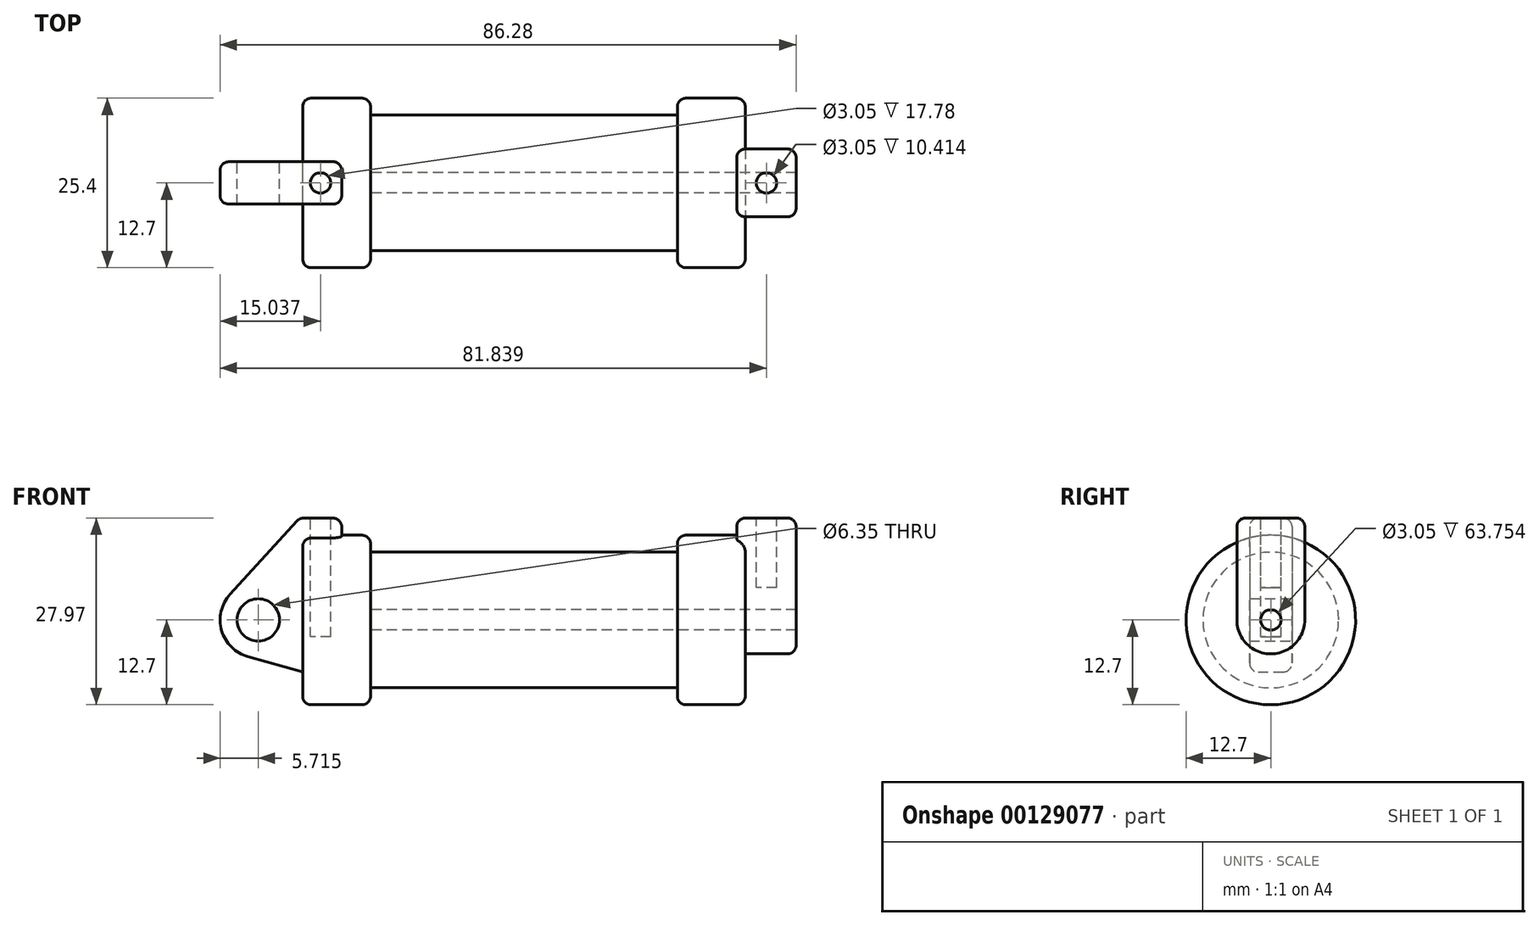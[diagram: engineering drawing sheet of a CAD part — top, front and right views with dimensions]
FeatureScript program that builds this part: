
annotation { "Feature Type Name" : "Feature", "Feature Type Description" : "" }
export const myFeature = defineFeature(function(context is Context, id is Id, definition is map)
    precondition{}
    {
        {
            var Q0;
            Q0=qCreatedBy(makeId("Front.planeOp"),FACE);
            var sketch = newSketch(context, id + "F0", { "sketchPlane" : qUnion([Q0])});
            skLineSegment(sketch, "E0", {"start": v(0, 0) * mm, "end": v(0, 12.7) * mm});
            skLineSegment(sketch, "E1", {"start": v(0, 12.7) * mm, "end": v(10.16, 12.7) * mm});
            skLineSegment(sketch, "E2", {"start": v(10.16, 12.7) * mm, "end": v(10.16, 10.16) * mm});
            skLineSegment(sketch, "E3", {"start": v(10.16, 10.16) * mm, "end": v(56.13, 10.16) * mm});
            skLineSegment(sketch, "E4", {"start": v(56.13, 10.16) * mm, "end": v(56.13, 12.7) * mm});
            skLineSegment(sketch, "E5", {"start": v(56.13, 12.7) * mm, "end": v(66.3, 12.7) * mm});
            skLineSegment(sketch, "E6", {"start": v(66.3, 12.7) * mm, "end": v(66.3, 0) * mm});
            skLineSegment(sketch, "E7", {"start": v(66.3, 0) * mm, "end": v(0, 0) * mm});
            skLineSegment(sketch, "E8", {"start": v(5.84, 15.24) * mm, "end": v(-0.5, 15.24) * mm});
            skLineSegment(sketch, "E9", {"start": v(-0.5, 15.24) * mm, "end": v(-10.88, 3.85) * mm});
            skLineSegment(sketch, "E10", {"start": v(0, 0) * mm, "end": v(-6.65, 0) * mm});
            skCircle(sketch, "E11", {"center": v(-6.65, 0) * mm, "radius": 5.72 * mm});
            skCircle(sketch, "E12", {"center": v(-6.65, 0) * mm, "radius": 3.18 * mm});
            skLineSegment(sketch, "E13", {"start": v(5.84, 15.24) * mm, "end": v(5.84, -9.4) * mm});
            skLineSegment(sketch, "E14", {"start": v(5.84, -9.4) * mm, "end": v(-8.18, -5.5) * mm});
            skSolve(sketch);
        }
        {
            var Q0;
            {var subQ0=sQuery(id+"F0.wireOp",EDGE,"E2");Q0=makeQuery(id+"F0.imprint","IMPRINT",FACE,{"disambiguationData":[TD([[makeQuery(id+"F0.imprint","IMPRINT",EDGE,{"derivedFrom":subQ0}),-1.0]])]});}
            var Q1;
            {var subQ0=sQuery(id+"F0.wireOp",EDGE,"E0");Q1=makeQuery(id+"F0.imprint","IMPRINT",FACE,{"disambiguationData":[TD([[makeQuery(id+"F0.imprint","IMPRINT",EDGE,{"derivedFrom":subQ0}),-1.0]])]});}
            var Q2;
            Q2=sQuery(id+"F0.wireOp",EDGE,"E7");
            revolve(context, id + "F1", {"entities" : qUnion([Q0, Q1]), "axis" : qUnion([Q2]), "revolveType" : RevolveType.FULL});
        }
        {
            var Q0;
            {var subQ4=sQuery(id+"F0.wireOp",EDGE,"E12");Q0=makeQuery(id+"F0.imprint","IMPRINT",FACE,{"disambiguationData":[TD([[makeQuery(id+"F0.imprint","IMPRINT",EDGE,{"derivedFrom":subQ4}),-1.0]])]});}
            var Q1;
            {var subQ0=sQuery(id+"F0.wireOp",EDGE,"E0");Q1=makeQuery(id+"F0.imprint","IMPRINT",FACE,{"disambiguationData":[TD([[makeQuery(id+"F0.imprint","IMPRINT",EDGE,{"derivedFrom":subQ0}),-1.0]])]});}
            var Q2;
            {var subQ3=sQuery(id+"F0.wireOp",EDGE,"E0");Q2=makeQuery(id+"F0.imprint","IMPRINT",FACE,{"disambiguationData":[TD([[makeQuery(id+"F0.imprint","IMPRINT",EDGE,{"derivedFrom":subQ3}),1.0]])]});}
            var Q3;
            {var subQ0=sQuery(id+"F0.wireOp",EDGE,"E14");Q3=makeQuery(id+"F0.imprint","IMPRINT",FACE,{"disambiguationData":[TD([[makeQuery(id+"F0.imprint","IMPRINT",EDGE,{"derivedFrom":subQ0}),-1.0]])]});}
            extrude(context, id + "F2", {"entities" : qUnion([Q0, Q1, Q2, Q3]), "operationType" : NewBodyOperationType.ADD, "endBound" : BoundingType.SYMMETRIC, "depth" : 6.35 * mm});
        }
        {
            var Q0;
            Q0=makeQuery(id+"F1.opRevolve","SWEPT_FACE",FACE,{"disambiguationData":[OSD([sQuery(id+"F0.wireOp",EDGE,"E6")])]});
            var sketch = newSketch(context, id + "F3", { "sketchPlane" : qUnion([Q0])});
            skCircle(sketch, "E15", {"center": v(0, 0) * mm, "radius": 1.52 * mm});
            skCircle(sketch, "E16", {"center": v(0, 0) * mm, "radius": 5.08 * mm});
            skLineSegment(sketch, "E17", {"start": v(-5.08, 0.03) * mm, "end": v(-5.08, 15.27) * mm});
            skLineSegment(sketch, "E18", {"start": v(-5.08, 15.27) * mm, "end": v(5.08, 15.27) * mm});
            skLineSegment(sketch, "E19", {"start": v(5.08, 15.27) * mm, "end": v(5.08, 0.03) * mm});
            skLineSegment(sketch, "E20", {"start": v(-1.52, -0.03) * mm, "end": v(1.52, -0.03) * mm});
            skSolve(sketch);
        }
        {
            var Q0;
            Q0 = qSketchRegion(id + "F3", true);
            extrude(context, id + "F4", {"entities" : qUnion([Q0]), "operationType" : NewBodyOperationType.ADD, "depth" : 7.62 * mm, "hasSecondDirection" : true, "secondDirectionOppositeDirection" : true, "secondDirectionDepth" : 1.27 * mm});
        }
        {
            var Q0;
            Q0=makeQuery(id+"F4.boolean.opBoolean","SPLIT",FACE,{"disambiguationData":[TD([makeQuery(id+"F4.opExtrude","SWEPT_FACE",FACE,{"disambiguationData":[OSD([sQuery(id+"F3.wireOp",EDGE,"E15")])]})])],"derivedFrom":makeQuery(id+"F1.opRevolve","SWEPT_FACE",FACE,{"disambiguationData":[OSD([sQuery(id+"F0.wireOp",EDGE,"E6")])]})});
            var Q1;
            Q1=makeQuery(id+"F1.opRevolve","SWEPT_FACE",FACE,{"disambiguationData":[OSD([sQuery(id+"F0.wireOp",EDGE,"E2")])]});
            extrude(context, id + "F5", {"entities" : qUnion([Q0]), "operationType" : NewBodyOperationType.REMOVE, "endBound" : BoundingType.UP_TO_SURFACE, "oppositeDirection" : true, "endBoundEntityFace" : qUnion([Q1]), "depth" : 25.4 * mm});
        }
        {
            var Q0;
            Q0=makeQuery(id+"F2.opExtrude","SWEPT_FACE",FACE,{"disambiguationData":[OSD([sQuery(id+"F0.wireOp",EDGE,"E8")])]});
            var sketch = newSketch(context, id + "F6", { "sketchPlane" : qUnion([Q0])});
            skCircle(sketch, "E21", {"center": v(2.67, 0) * mm, "radius": 1.52 * mm});
            skPoint(sketch, "E21.centerSnap0", {"position": v(2.67, 3.18) * mm});
            skSolve(sketch);
        }
        {
            var Q0;
            Q0=makeQuery(id+"F4.opExtrude","SWEPT_FACE",FACE,{"disambiguationData":[OSD([sQuery(id+"F3.wireOp",EDGE,"E18")])]});
            var sketch = newSketch(context, id + "F7", { "sketchPlane" : qUnion([Q0])});
            skCircle(sketch, "E22", {"center": v(69.47, 0) * mm, "radius": 1.52 * mm});
            skSolve(sketch);
        }
        {
            var Q0;
            Q0=makeQuery(id+"F6.imprint","IMPRINT",FACE,{"disambiguationData":[TD([[makeQuery(id+"F6.imprint","IMPRINT",EDGE,{"derivedFrom":sQuery(id+"F6.wireOp",EDGE,"E21")}),1.0]])]});
            extrude(context, id + "F8", {"entities" : qUnion([Q0]), "operationType" : NewBodyOperationType.REMOVE, "oppositeDirection" : true, "depth" : 17.78 * mm});
        }
        {
            var Q0;
            Q0=makeQuery(id+"F7.imprint","IMPRINT",FACE,{"disambiguationData":[TD([[makeQuery(id+"F7.imprint","IMPRINT",EDGE,{"derivedFrom":sQuery(id+"F7.wireOp",EDGE,"E22")}),1.0]])]});
            extrude(context, id + "F9", {"entities" : qUnion([Q0]), "operationType" : NewBodyOperationType.REMOVE, "oppositeDirection" : true, "depth" : 10.4 * mm});
        }
        {
            var Q0;
            Q0=makeQuery(id+"F2.opExtrude","CAP_EDGE",EDGE,{"disambiguationData":[OSD([sQuery(id+"F0.wireOp",EDGE,"E8")])],"isStart":false});
            var Q1;
            Q1=makeQuery(id+"F2.opExtrude","SWEPT_EDGE",EDGE,{"disambiguationData":[OSD([sQuery(id+"F0.wireOp",EDGE,"E8"),sQuery(id+"F0.wireOp",EDGE,"E9")])]});
            var Q2;
            Q2=makeQuery(id+"F2.opExtrude","CAP_EDGE",EDGE,{"disambiguationData":[OSD([sQuery(id+"F0.wireOp",EDGE,"E8")])],"isStart":true});
            var Q3;
            Q3=makeQuery(id+"F2.opExtrude","SWEPT_EDGE",EDGE,{"disambiguationData":[OSD([sQuery(id+"F0.wireOp",EDGE,"E8"),sQuery(id+"F0.wireOp",EDGE,"E13")])]});
            var Q4;
            Q4=makeQuery(id+"F2.opExtrude","CAP_EDGE",EDGE,{"disambiguationData":[OSD([sQuery(id+"F0.wireOp",EDGE,"E13")])],"isStart":true});
            var Q5;
            Q5=makeQuery(id+"F2.opExtrude","CAP_EDGE",EDGE,{"disambiguationData":[OSD([sQuery(id+"F0.wireOp",EDGE,"E13")])],"isStart":false});
            var Q6;
            Q6=makeQuery(id+"F2.opExtrude","CAP_EDGE",EDGE,{"disambiguationData":[OSD([sQuery(id+"F0.wireOp",EDGE,"E9")])],"isStart":true});
            var Q7;
            Q7=makeQuery(id+"F2.opExtrude","CAP_EDGE",EDGE,{"disambiguationData":[OSD([sQuery(id+"F0.wireOp",EDGE,"E9")])],"isStart":false});
            var Q8;
            Q8=makeQuery(id+"F1.opRevolve","SWEPT_EDGE",EDGE,{"disambiguationData":[OSD([sQuery(id+"F0.wireOp",EDGE,"E0"),sQuery(id+"F0.wireOp",EDGE,"E1")])]});
            var Q9;
            Q9=makeQuery(id+"F1.opRevolve","SWEPT_EDGE",EDGE,{"disambiguationData":[OSD([sQuery(id+"F0.wireOp",EDGE,"E1"),sQuery(id+"F0.wireOp",EDGE,"E2")])]});
            var Q10;
            Q10=makeQuery(id+"F1.opRevolve","SWEPT_EDGE",EDGE,{"disambiguationData":[OSD([sQuery(id+"F0.wireOp",EDGE,"E4"),sQuery(id+"F0.wireOp",EDGE,"E5")])]});
            var Q11;
            Q11=makeQuery(id+"F1.opRevolve","SWEPT_EDGE",EDGE,{"disambiguationData":[OSD([sQuery(id+"F0.wireOp",EDGE,"E5"),sQuery(id+"F0.wireOp",EDGE,"E6")])]});
            var Q12;
            Q12=makeQuery(id+"F4.opExtrude","SWEPT_EDGE",EDGE,{"disambiguationData":[OSD([sQuery(id+"F3.wireOp",EDGE,"E18"),sQuery(id+"F3.wireOp",EDGE,"E19")])]});
            var Q13;
            Q13=makeQuery(id+"F4.opExtrude","SWEPT_EDGE",EDGE,{"disambiguationData":[OSD([sQuery(id+"F3.wireOp",EDGE,"E17"),sQuery(id+"F3.wireOp",EDGE,"E18")])]});
            var Q14;
            Q14=makeQuery(id+"F4.opExtrude","CAP_EDGE",EDGE,{"disambiguationData":[OSD([sQuery(id+"F3.wireOp",EDGE,"E18")])],"isStart":false});
            var Q15;
            Q15=makeQuery(id+"F4.opExtrude","CAP_EDGE",EDGE,{"disambiguationData":[OSD([sQuery(id+"F3.wireOp",EDGE,"E18")])],"isStart":true});
            var Q16;
            Q16=makeQuery(id+"F4.opExtrude","CAP_EDGE",EDGE,{"disambiguationData":[OSD([sQuery(id+"F3.wireOp",EDGE,"E19")])],"isStart":false});
            var Q17;
            Q17=makeQuery(id+"F4.opExtrude","CAP_EDGE",EDGE,{"disambiguationData":[OSD([sQuery(id+"F3.wireOp",EDGE,"E17")])],"isStart":false});
            var Q18;
            Q18=makeQuery(id+"F4.opExtrude","CAP_EDGE",EDGE,{"disambiguationData":[OSD([sQuery(id+"F3.wireOp",EDGE,"E16")])],"isStart":false});
            fillet(context, id + "F10", {"entities" : qUnion([Q0, Q1, Q2, Q3, Q4, Q5, Q6, Q7, Q8, Q9, Q10, Q11, Q12, Q13, Q14, Q15, Q16, Q17, Q18]), "radius" : 1.27 * mm, "tangentPropagation" : true, "allowEdgeOverflow" : false});
        }
        {
            var Q0;
            Q0=makeQuery(id+"F4.opExtrude","CAP_EDGE",EDGE,{"disambiguationData":[OSD([sQuery(id+"F3.wireOp",EDGE,"E17")])],"isStart":true});
            var Q1;
            Q1=makeQuery(id+"F4.opExtrude","CAP_EDGE",EDGE,{"disambiguationData":[OSD([sQuery(id+"F3.wireOp",EDGE,"E19")])],"isStart":true});
            fillet(context, id + "F11", {"entities" : qUnion([Q0, Q1]), "radius" : 1.27 * mm, "tangentPropagation" : true, "allowEdgeOverflow" : false});
        }
    });
